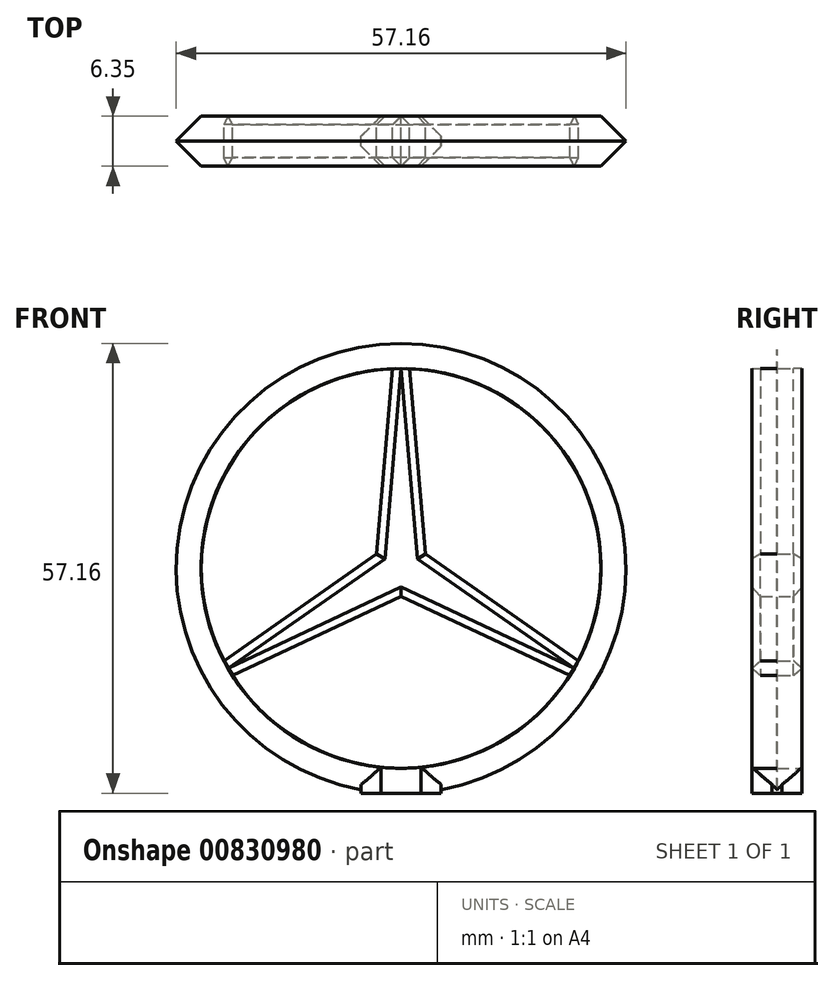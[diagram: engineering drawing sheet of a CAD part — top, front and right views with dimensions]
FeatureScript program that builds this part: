
annotation { "Feature Type Name" : "Feature", "Feature Type Description" : "" }
export const myFeature = defineFeature(function(context is Context, id is Id, definition is map)
    precondition{}
    {
        {
            var Q0;
            Q0=qCreatedBy(makeId("Front.planeOp"),FACE);
            var sketch = newSketch(context, id + "F0", { "sketchPlane" : qUnion([Q0])});
            skCircle(sketch, "E0", {"center": v(0, 0) * mm, "radius": 25.4 * mm});
            skCircle(sketch, "E1", {"center": v(0, 0) * mm, "radius": 28.58 * mm});
            skLineSegment(sketch, "E2", {"start": v(-1.09, 25.38) * mm, "end": v(-2.54, 8.38) * mm});
            skLineSegment(sketch, "E3", {"start": v(2.54, 8.38) * mm, "end": v(1.09, 25.38) * mm});
            skPoint(sketch, "E4.orphan", {"position": v(0, 38.1) * mm});
            skLineSegment(sketch, "E5.1.0", {"start": v(-21.43, -13.63) * mm, "end": v(-5.99, -6.4) * mm});
            skLineSegment(sketch, "E5.1.1", {"start": v(-8.53, -2) * mm, "end": v(-22.52, -11.75) * mm});
            skLineSegment(sketch, "E5.2.0", {"start": v(22.52, -11.75) * mm, "end": v(8.53, -2) * mm});
            skLineSegment(sketch, "E5.2.1", {"start": v(5.99, -6.4) * mm, "end": v(21.43, -13.63) * mm});
            skLineSegment(sketch, "E6", {"start": v(-2.54, 8.38) * mm, "end": v(-3.1, 1.8) * mm});
            skLineSegment(sketch, "E7", {"start": v(-8.53, -2) * mm, "end": v(-3.1, 1.8) * mm});
            skLineSegment(sketch, "E8", {"start": v(-5.99, -6.4) * mm, "end": v(0, -3.58) * mm});
            skLineSegment(sketch, "E9", {"start": v(5.99, -6.4) * mm, "end": v(0, -3.58) * mm});
            skLineSegment(sketch, "E10", {"start": v(8.53, -2) * mm, "end": v(3.1, 1.8) * mm});
            skLineSegment(sketch, "E11", {"start": v(2.54, 8.38) * mm, "end": v(3.1, 1.8) * mm});
            skPoint(sketch, "E12.start.orphan", {"position": v(0, 8.38) * mm});
            skLineSegment(sketch, "E13", {"start": v(0, -28.58) * mm, "end": v(-5.08, -28.58) * mm});
            skLineSegment(sketch, "E14", {"start": v(-5.08, -28.58) * mm, "end": v(5.08, -28.58) * mm});
            skLineSegment(sketch, "E15", {"start": v(5.08, -28.58) * mm, "end": v(5.08, -28.12) * mm});
            skLineSegment(sketch, "E16", {"start": v(-5.08, -28.58) * mm, "end": v(-5.08, -28.12) * mm});
            skSolve(sketch);
        }
        {
            var Q0;
            Q0 = qSketchRegion(id + "F0", true);
            var Q1;
            {var subQ5=sQuery(id+"F0.wireOp",EDGE,"E2");Q1=makeQuery(id+"F0.imprint","IMPRINT",FACE,{"disambiguationData":[TD([[makeQuery(id+"F0.imprint","IMPRINT",EDGE,{"derivedFrom":subQ5}),1.0]])]});}
            extrude(context, id + "F1", {"entities" : qUnion([Q0, Q1]), "depth" : 6.35 * mm, "offsetDistance" : 25.4 * mm});
        }
        {
            var Q0;
            Q0=makeQuery(id+"F1.opExtrude","CAP_EDGE",EDGE,{"disambiguationData":[OSD([sQuery(id+"F0.wireOp",EDGE,"E1")])],"isStart":false});
            var Q1;
            Q1=makeQuery(id+"F1.opExtrude","CAP_EDGE",EDGE,{"disambiguationData":[OSD([sQuery(id+"F0.wireOp",EDGE,"E1")])],"isStart":true});
            chamfer(context, id + "F2", {"entities" : qUnion([Q0, Q1]), "width" : 3.17 * mm, "tangentPropagation" : true});
        }
        {
            var Q0;
            Q0=makeQuery(id+"F1.opExtrude","CAP_EDGE",EDGE,{"disambiguationData":[OSD([sQuery(id+"F0.wireOp",EDGE,"E16")])],"isStart":false});
            var Q1;
            Q1=makeQuery(id+"F1.opExtrude","CAP_EDGE",EDGE,{"disambiguationData":[OSD([sQuery(id+"F0.wireOp",EDGE,"E15")])],"isStart":false});
            var Q2;
            Q2=makeQuery(id+"F1.opExtrude","CAP_EDGE",EDGE,{"disambiguationData":[OSD([sQuery(id+"F0.wireOp",EDGE,"E15")])],"isStart":true});
            var Q3;
            Q3=makeQuery(id+"F1.opExtrude","CAP_EDGE",EDGE,{"disambiguationData":[OSD([sQuery(id+"F0.wireOp",EDGE,"E16")])],"isStart":true});
            chamfer(context, id + "F3", {"entities" : qUnion([Q0, Q1, Q2, Q3]), "width" : 2.54 * mm, "tangentPropagation" : true});
        }
        {
            var Q0;
            Q0=makeQuery(id+"F1.opExtrude","CAP_EDGE",EDGE,{"disambiguationData":[OSD([sQuery(id+"F0.wireOp",EDGE,"E2"),sQuery(id+"F0.wireOp",EDGE,"E6")])],"isStart":true});
            var Q1;
            Q1=makeQuery(id+"F1.opExtrude","CAP_EDGE",EDGE,{"disambiguationData":[OSD([sQuery(id+"F0.wireOp",EDGE,"E5.2.0"),sQuery(id+"F0.wireOp",EDGE,"E10")])],"isStart":true});
            var Q2;
            Q2=makeQuery(id+"F1.opExtrude","CAP_EDGE",EDGE,{"disambiguationData":[OSD([sQuery(id+"F0.wireOp",EDGE,"E5.1.1"),sQuery(id+"F0.wireOp",EDGE,"E7")])],"isStart":true});
            var Q3;
            Q3=makeQuery(id+"F1.opExtrude","CAP_EDGE",EDGE,{"disambiguationData":[OSD([sQuery(id+"F0.wireOp",EDGE,"E5.1.0"),sQuery(id+"F0.wireOp",EDGE,"E8")])],"isStart":true});
            var Q4;
            Q4=makeQuery(id+"F1.opExtrude","CAP_EDGE",EDGE,{"disambiguationData":[OSD([sQuery(id+"F0.wireOp",EDGE,"E5.2.1"),sQuery(id+"F0.wireOp",EDGE,"E9")])],"isStart":true});
            var Q5;
            Q5=makeQuery(id+"F1.opExtrude","CAP_EDGE",EDGE,{"disambiguationData":[OSD([sQuery(id+"F0.wireOp",EDGE,"E5.2.0"),sQuery(id+"F0.wireOp",EDGE,"E10")])],"isStart":false});
            var Q6;
            Q6=makeQuery(id+"F1.opExtrude","CAP_EDGE",EDGE,{"disambiguationData":[OSD([sQuery(id+"F0.wireOp",EDGE,"E3"),sQuery(id+"F0.wireOp",EDGE,"E11")])],"isStart":true});
            var Q7;
            Q7=makeQuery(id+"F1.opExtrude","CAP_EDGE",EDGE,{"disambiguationData":[OSD([sQuery(id+"F0.wireOp",EDGE,"E3"),sQuery(id+"F0.wireOp",EDGE,"E11")])],"isStart":false});
            var Q8;
            Q8=makeQuery(id+"F1.opExtrude","CAP_EDGE",EDGE,{"disambiguationData":[OSD([sQuery(id+"F0.wireOp",EDGE,"E2"),sQuery(id+"F0.wireOp",EDGE,"E6")])],"isStart":false});
            var Q9;
            Q9=makeQuery(id+"F1.opExtrude","CAP_EDGE",EDGE,{"disambiguationData":[OSD([sQuery(id+"F0.wireOp",EDGE,"E5.1.1"),sQuery(id+"F0.wireOp",EDGE,"E7")])],"isStart":false});
            var Q10;
            Q10=makeQuery(id+"F1.opExtrude","CAP_EDGE",EDGE,{"disambiguationData":[OSD([sQuery(id+"F0.wireOp",EDGE,"E5.2.1"),sQuery(id+"F0.wireOp",EDGE,"E9")])],"isStart":false});
            var Q11;
            Q11=makeQuery(id+"F1.opExtrude","CAP_EDGE",EDGE,{"disambiguationData":[OSD([sQuery(id+"F0.wireOp",EDGE,"E5.1.0"),sQuery(id+"F0.wireOp",EDGE,"E8")])],"isStart":false});
            chamfer(context, id + "F4", {"entities" : qUnion([Q0, Q1, Q2, Q3, Q4, Q5, Q6, Q7, Q8, Q9, Q10, Q11]), "width" : 1.08 * mm, "tangentPropagation" : true});
        }
    });
